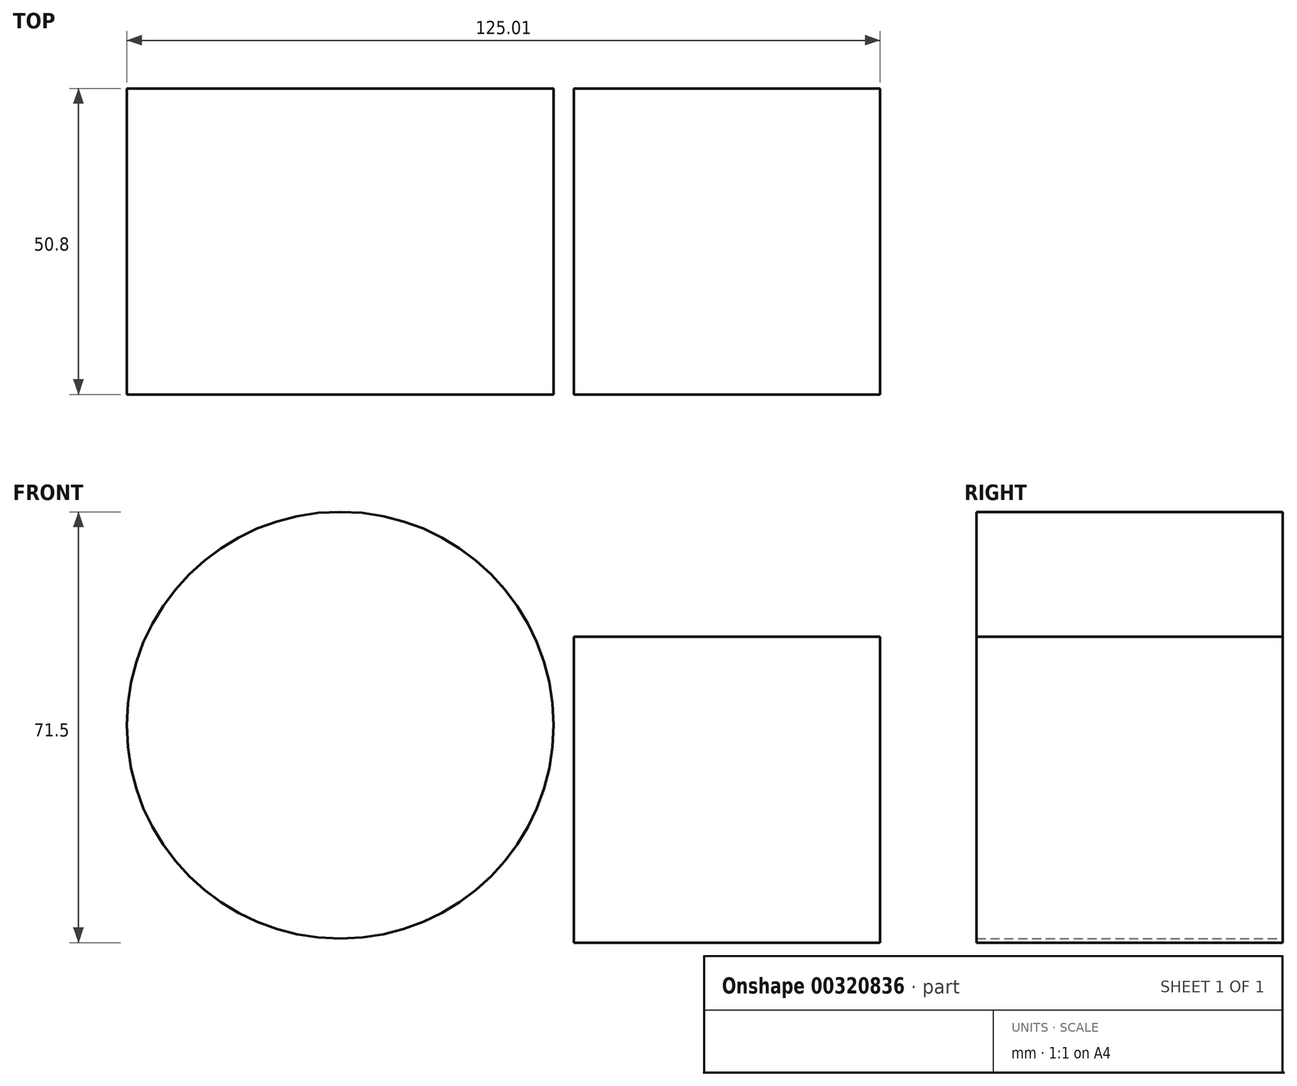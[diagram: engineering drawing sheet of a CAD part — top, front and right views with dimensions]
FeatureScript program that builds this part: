
annotation { "Feature Type Name" : "Feature", "Feature Type Description" : "" }
export const myFeature = defineFeature(function(context is Context, id is Id, definition is map)
    precondition{}
    {
        {
            var Q0;
            Q0=qCreatedBy(makeId("Front.planeOp"),FACE);
            var sketch = newSketch(context, id + "F0", { "sketchPlane" : qUnion([Q0])});
            skLineSegment(sketch, "E0.bottom", {"start": v(0, 0) * mm, "end": v(50.8, 0) * mm});
            skLineSegment(sketch, "E0.top", {"start": v(0, 50.8) * mm, "end": v(50.8, 50.8) * mm});
            skLineSegment(sketch, "E0.left", {"start": v(0, 0) * mm, "end": v(0, 50.8) * mm});
            skLineSegment(sketch, "E0.right", {"start": v(50.8, 0) * mm, "end": v(50.8, 50.8) * mm});
            skSolve(sketch);
        }
        {
            var Q0;
            Q0 = qSketchRegion(id + "F0", true);
            extrude(context, id + "F1", {"entities" : qUnion([Q0]), "depth" : 50.8 * mm});
        }
        {
            var Q0;
            Q0=qCreatedBy(makeId("Front.planeOp"),FACE);
            var sketch = newSketch(context, id + "F2", { "sketchPlane" : qUnion([Q0])});
            skCircle(sketch, "E1", {"center": v(-38.79, 36.08) * mm, "radius": 35.42 * mm});
            skSolve(sketch);
        }
        {
            var Q0;
            Q0 = qSketchRegion(id + "F2", true);
            extrude(context, id + "F3", {"entities" : qUnion([Q0]), "depth" : 50.8 * mm});
        }
        {
            var Q0;
            Q0=qCreatedBy(makeId("Front.planeOp"),FACE);
            var sketch = newSketch(context, id + "F4", { "sketchPlane" : qUnion([Q0])});
            skLineSegment(sketch, "E2", {"start": v(0, 0) * mm, "end": v(0, -76.2) * mm});
            skArc(sketch, "E3", {"start": v(0, 0) * mm, "mid": v(-38.16, -38.1) * mm, "end": v(0, -76.2) * mm});
            skSolve(sketch);
        }
        {
            var Q0;
            Q0=makeQuery(id+"F4.imprint","IMPRINT",FACE,{"disambiguationData":[TD([[makeQuery(id+"F4.imprint","IMPRINT",EDGE,{"derivedFrom":sQuery(id+"F4.wireOp",EDGE,"E2")}),-1.0]])]});
            var Q1;
            Q1=sQuery(id+"F4.wireOp",EDGE,"E2");
            revolve(context, id + "F5", {"operationType" : NewBodyOperationType.ADD, "entities" : qUnion([Q0]), "axis" : qUnion([Q1]), "revolveType" : RevolveType.FULL});
        }
    });
